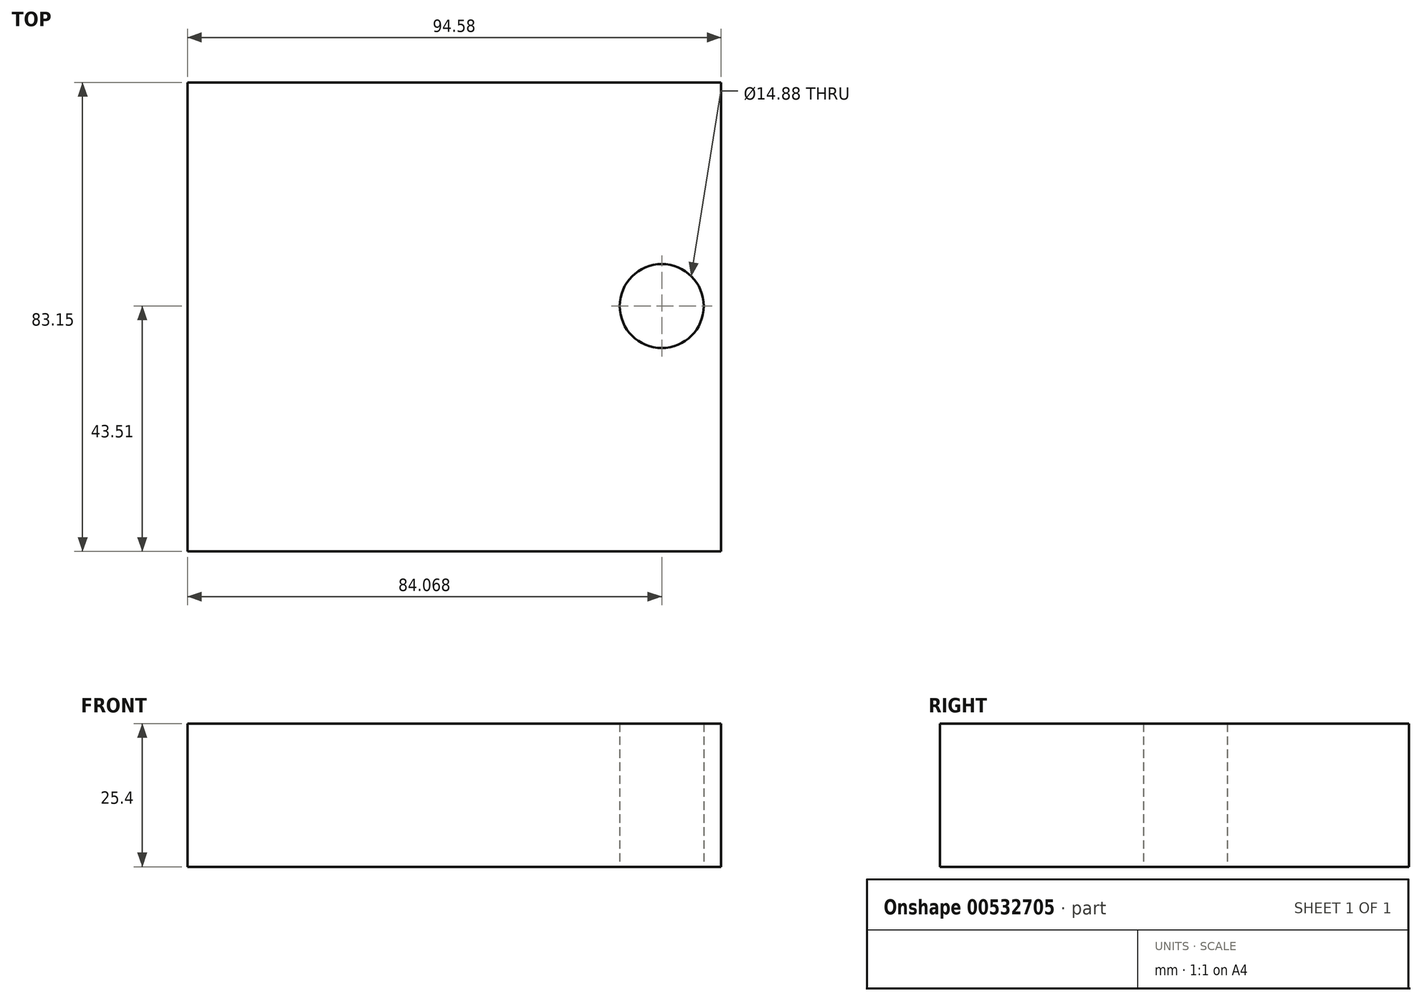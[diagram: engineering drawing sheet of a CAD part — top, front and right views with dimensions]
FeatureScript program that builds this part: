
annotation { "Feature Type Name" : "Feature", "Feature Type Description" : "" }
export const myFeature = defineFeature(function(context is Context, id is Id, definition is map)
    precondition{}
    {
        {
            var Q0;
            Q0=qCreatedBy(makeId("Top.planeOp"),FACE);
            var sketch = newSketch(context, id + "F0", { "sketchPlane" : qUnion([Q0])});
            skLineSegment(sketch, "E0.bottom", {"start": v(0, -43.5) * mm, "end": v(-46.46, -43.5) * mm});
            skLineSegment(sketch, "E0.top", {"start": v(0, 39.64) * mm, "end": v(-46.46, 39.64) * mm});
            skLineSegment(sketch, "E0.left", {"start": v(0, -43.5) * mm, "end": v(0, 39.64) * mm});
            skLineSegment(sketch, "E0.right", {"start": v(-46.46, -43.5) * mm, "end": v(-46.46, 39.64) * mm});
            skLineSegment(sketch, "E1.bottom", {"start": v(0, 39.64) * mm, "end": v(48.12, 39.64) * mm});
            skLineSegment(sketch, "E1.top", {"start": v(0, -43.5) * mm, "end": v(48.12, -43.5) * mm});
            skLineSegment(sketch, "E1.left", {"start": v(0, 39.64) * mm, "end": v(0, -43.5) * mm});
            skLineSegment(sketch, "E1.right", {"start": v(48.12, 39.64) * mm, "end": v(48.12, -43.5) * mm});
            skCircle(sketch, "E2", {"center": v(37.6, 0) * mm, "radius": 7.44 * mm});
            skSolve(sketch);
        }
        {
            var Q0;
            Q0 = qSketchRegion(id + "F0", true);
            extrude(context, id + "F1", {"entities" : qUnion([Q0]), "depth" : 25.4 * mm, "offsetDistance" : 25.4 * mm});
        }
        {
            var Q0;
            Q0=makeQuery(id+"F1.opExtrude","CAP_FACE",FACE,{"disambiguationData":[OSD([sQuery(id+"F0.wireOp",EDGE,"E0.bottom"),sQuery(id+"F0.wireOp",EDGE,"E0.top"),sQuery(id+"F0.wireOp",EDGE,"E0.right"),sQuery(id+"F0.wireOp",EDGE,"E1.bottom"),sQuery(id+"F0.wireOp",EDGE,"E1.top"),sQuery(id+"F0.wireOp",EDGE,"E1.right"),sQuery(id+"F0.wireOp",EDGE,"E2")])],"isStart":false});
            var sketch = newSketch(context, id + "F2", { "sketchPlane" : qUnion([Q0])});
            skLineSegment(sketch, "E3", {"start": v(-37.24, 0) * mm, "end": v(37.6, 0) * mm});
            skSolve(sketch);
        }
        {
            var Q0;
            Q0=sQuery(id+"F2.wireOp",EDGE,"E3");
            extrude(context, id + "F3", {"bodyType" : ToolBodyType.SURFACE, "surfaceEntities" : qUnion([Q0]), "depth" : 50.8 * mm, "offsetDistance" : 25.4 * mm});
        }
        {
            var Q0;
            Q0=makeQuery(id+"F3.opExtrude","SWEPT_FACE",FACE,{"disambiguationData":[OSD([sQuery(id+"F2.wireOp",EDGE,"E3")])]});
            var sketch = newSketch(context, id + "F4", { "sketchPlane" : qUnion([Q0])});
            skFitSpline(sketch, "E4", {"points": [v(-37.24, 25.4) * mm, v(-32.6, 58.06) * mm, v(-15.86, 72.19) * mm, v(0, 73.79) * mm, v(21.54, 73.79) * mm, v(33.57, 65.3) * mm, v(37.6, 25.4) * mm], "startDerivative": vector(0.23, 182.66) * mm, "endDerivative": vector(-1.15, -217.95) * mm});
            skSolve(sketch);
        }
        {
            var Q0;
            Q0=makeQuery(id+"F3.opExtrude","SWEPT_BODY",BODY,{"disambiguationData":[OSD([sQuery(id+"F2.wireOp",EDGE,"E3")])]});
            deleteBodies(context, id + "F5", {"entities" : qUnion([Q0])});
        }
    });
